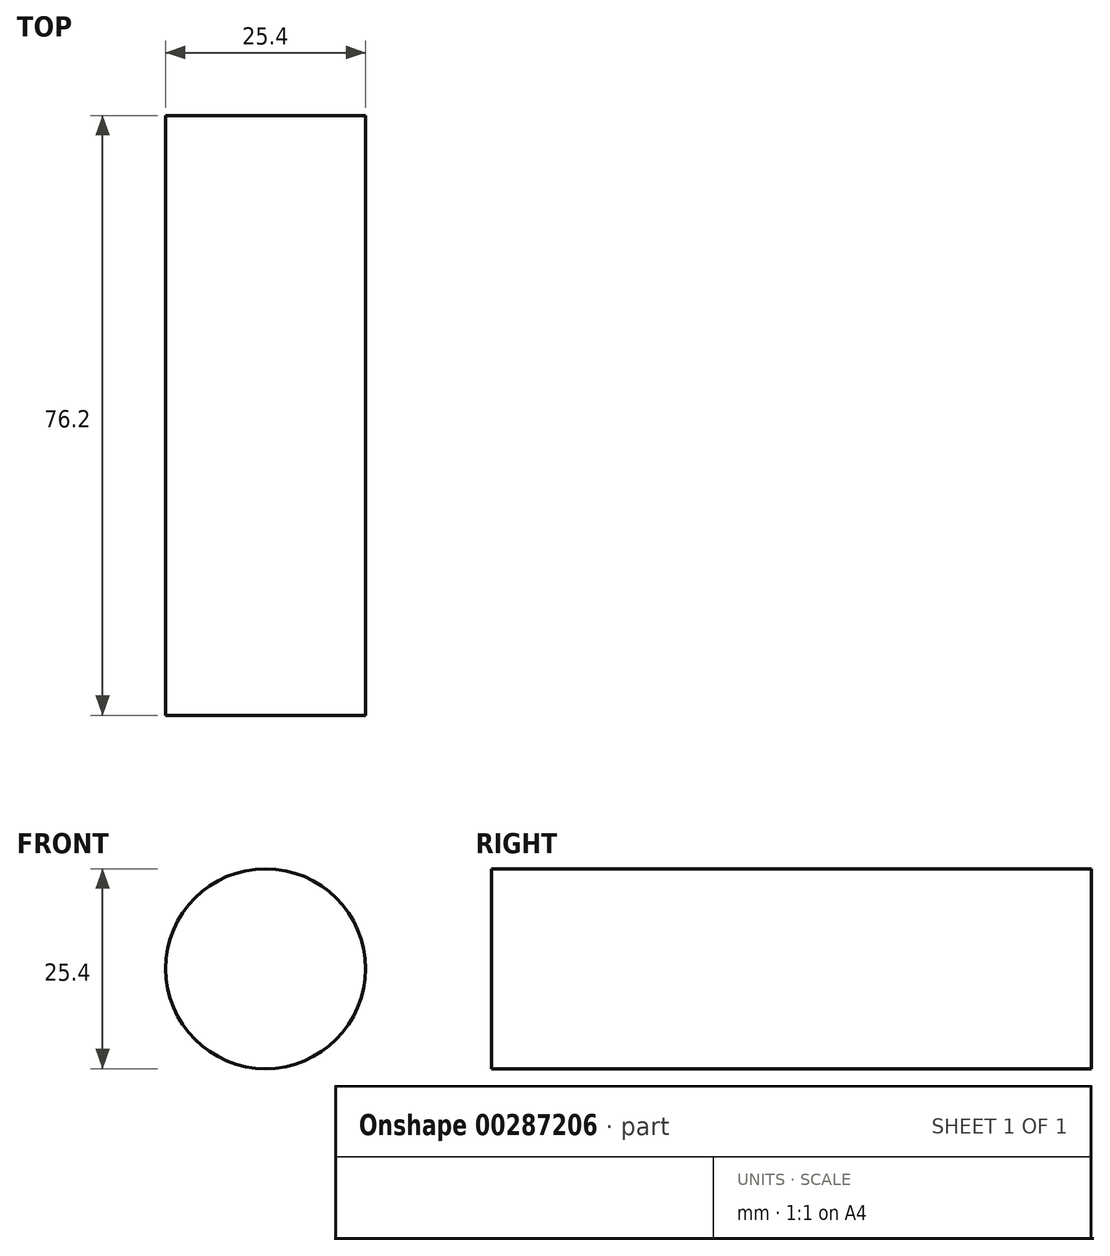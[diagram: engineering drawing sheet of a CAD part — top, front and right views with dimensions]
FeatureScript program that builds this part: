
annotation { "Feature Type Name" : "Feature", "Feature Type Description" : "" }
export const myFeature = defineFeature(function(context is Context, id is Id, definition is map)
    precondition{}
    {
        {
            var Q0;
            Q0=qCreatedBy(makeId("Front.planeOp"),FACE);
            var sketch = newSketch(context, id + "F0", { "sketchPlane" : qUnion([Q0])});
            skCircle(sketch, "E0", {"center": v(0, 1.72) * mm, "radius": 12.7 * mm});
            skSolve(sketch);
        }
        {
            var Q0;
            Q0 = qSketchRegion(id + "F0", true);
            extrude(context, id + "F1", {"entities" : qUnion([Q0]), "depth" : 76.2 * mm});
        }
    });
